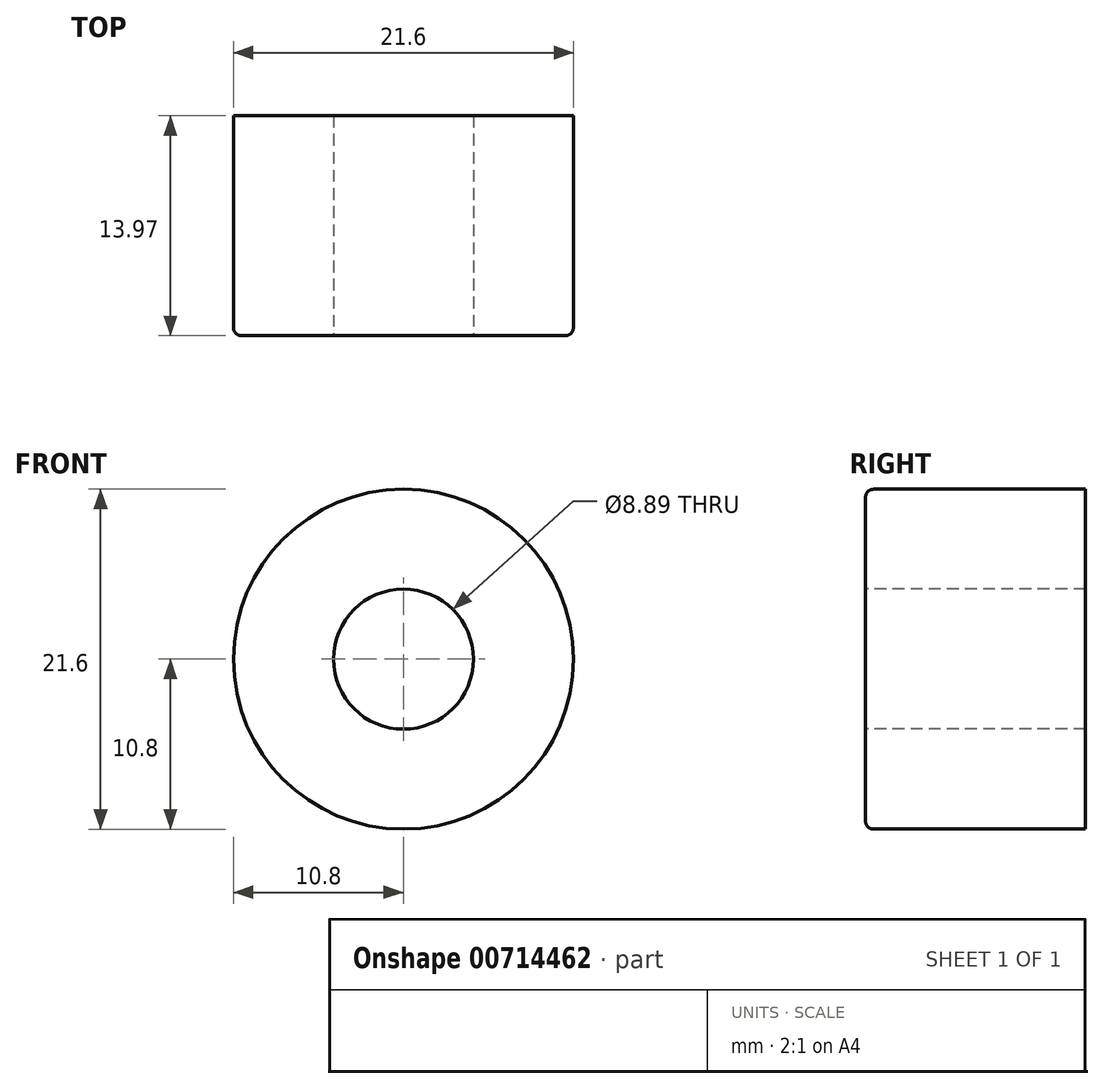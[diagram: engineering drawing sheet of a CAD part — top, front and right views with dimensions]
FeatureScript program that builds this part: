
annotation { "Feature Type Name" : "Feature", "Feature Type Description" : "" }
export const myFeature = defineFeature(function(context is Context, id is Id, definition is map)
    precondition{}
    {
        {
            var Q0;
            Q0=qCreatedBy(makeId("Front.planeOp"),FACE);
            var sketch = newSketch(context, id + "F0", { "sketchPlane" : qUnion([Q0])});
            skCircle(sketch, "E0", {"center": v(0, 0) * mm, "radius": 10.8 * mm});
            skSolve(sketch);
        }
        {
            var Q0;
            Q0 = qSketchRegion(id + "F0", true);
            extrude(context, id + "F1", {"entities" : qUnion([Q0]), "depth" : 13.97 * mm, "offsetDistance" : 25.4 * mm});
        }
        {
            var Q0;
            Q0=makeQuery(id+"F1.opExtrude","CAP_FACE",FACE,{"disambiguationData":[OSD([sQuery(id+"F0.wireOp",EDGE,"E0")])],"isStart":false});
            var sketch = newSketch(context, id + "F2", { "sketchPlane" : qUnion([Q0])});
            skCircle(sketch, "E1", {"center": v(0, 0) * mm, "radius": 4.45 * mm});
            skSolve(sketch);
        }
        {
            var Q0;
            Q0 = qSketchRegion(id + "F2", true);
            extrude(context, id + "F3", {"entities" : qUnion([Q0]), "operationType" : NewBodyOperationType.REMOVE, "oppositeDirection" : true, "depth" : 25.4 * mm, "offsetDistance" : 25.4 * mm});
        }
        {
            var Q0;
            Q0=makeQuery(id+"F1.opExtrude","CAP_EDGE",EDGE,{"disambiguationData":[OSD([sQuery(id+"F0.wireOp",EDGE,"E0")])],"isStart":false});
            fillet(context, id + "F4", {"entities" : qUnion([Q0]), "radius" : 0.5 * mm, "tangentPropagation" : true, "allowEdgeOverflow" : false});
        }
    });
